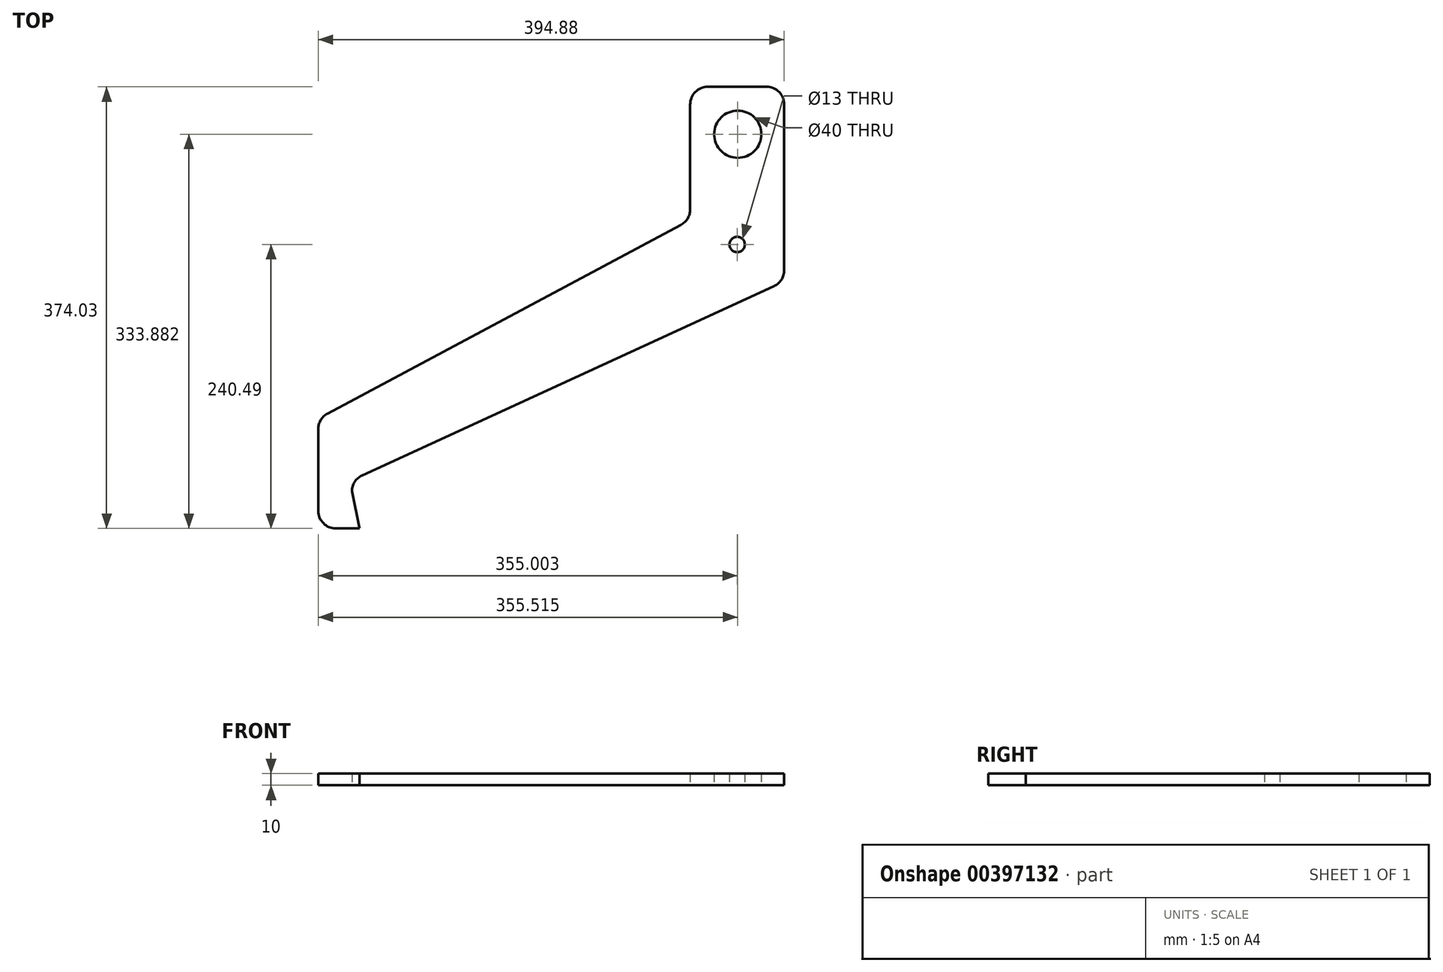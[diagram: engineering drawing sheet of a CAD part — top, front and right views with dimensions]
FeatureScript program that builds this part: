
annotation { "Feature Type Name" : "Feature", "Feature Type Description" : "" }
export const myFeature = defineFeature(function(context is Context, id is Id, definition is map)
    precondition{}
    {
        {
            var Q0;
            Q0=qCreatedBy(makeId("Top.planeOp"),FACE);
            var sketch = newSketch(context, id + "F0", { "sketchPlane" : qUnion([Q0])});
            skLineSegment(sketch, "E0.left", {"start": v(210.78, 66.79) * mm, "end": v(188.14, 86.98) * mm, "construction": true});
            skPoint(sketch, "E0.middle", {"position": v(0, 0) * mm});
            skLineSegment(sketch, "E1", {"start": v(-206.28, -210.92) * mm, "end": v(349.58, -210.92) * mm});
            skLineSegment(sketch, "E2", {"start": v(-160.53, -111.6) * mm, "end": v(-160.53, -210.92) * mm});
            skLineSegment(sketch, "E3.bottom", {"start": v(213.87, 220.23) * mm, "end": v(163.87, 220.5) * mm, "construction": true});
            skLineSegment(sketch, "E3.left", {"start": v(228.8, 205.15) * mm, "end": v(228.02, 65.27) * mm, "construction": true});
            skLineSegment(sketch, "E3.right", {"start": v(148.8, 205.6) * mm, "end": v(148.3, 116.66) * mm, "construction": true});
            skLineSegment(sketch, "E4", {"start": v(-158.92, -56.19) * mm, "end": v(140.37, 103.5) * mm});
            skLineSegment(sketch, "E5", {"start": v(-129.58, -108.53) * mm, "end": v(219.29, 51.72) * mm});
            skLineSegment(sketch, "E6", {"start": v(148.3, 116.66) * mm, "end": v(148.3, 205.52) * mm});
            skLineSegment(sketch, "E7", {"start": v(163.3, 220.52) * mm, "end": v(213.02, 220.52) * mm});
            skLineSegment(sketch, "E8", {"start": v(228.02, 205.52) * mm, "end": v(228.02, 65.27) * mm});
            skCircle(sketch, "E9", {"center": v(188.66, 180.37) * mm, "radius": 20 * mm});
            skLineSegment(sketch, "E10", {"start": v(-166.86, -69.42) * mm, "end": v(-166.86, -138.5) * mm});
            skLineSegment(sketch, "E11", {"start": v(-151.86, -153.5) * mm, "end": v(-142.06, -153.5) * mm});
            skCircle(sketch, "E12", {"center": v(188.14, 86.98) * mm, "radius": 6.5 * mm});
            skArc(sketch, "E13.filletArc", {"start": v(219.29, 51.72) * mm, "mid": v(225.63, 57.22) * mm, "end": v(228.02, 65.27) * mm});
            skArc(sketch, "E14.filletArc", {"start": v(140.37, 103.5) * mm, "mid": v(146.15, 108.99) * mm, "end": v(148.3, 116.66) * mm});
            skArc(sketch, "E15.filletArc", {"start": v(-158.92, -56.19) * mm, "mid": v(-164.72, -61.7) * mm, "end": v(-166.86, -69.42) * mm});
            skArc(sketch, "E16.filletArc", {"start": v(-129.58, -108.53) * mm, "mid": v(-135.86, -113.93) * mm, "end": v(-138.31, -121.85) * mm});
            skArc(sketch, "E17.filletArc", {"start": v(163.3, 220.52) * mm, "mid": v(152.7, 216.13) * mm, "end": v(148.3, 205.52) * mm});
            skArc(sketch, "E18.filletArc", {"start": v(228.02, 205.52) * mm, "mid": v(223.63, 216.13) * mm, "end": v(213.02, 220.52) * mm});
            skArc(sketch, "E19.filletArc", {"start": v(-166.86, -138.5) * mm, "mid": v(-162.46, -149.11) * mm, "end": v(-151.86, -153.5) * mm});
            skLineSegment(sketch, "E20", {"start": v(188.14, 86.98) * mm, "end": v(188.14, -254.15) * mm, "construction": true});
            skLineSegment(sketch, "E21", {"start": v(-138.31, -121.85) * mm, "end": v(-131.86, -153.5) * mm});
            skLineSegment(sketch, "E22", {"start": v(-131.86, -153.5) * mm, "end": v(-142.06, -153.5) * mm});
            skPoint(sketch, "E23.orphan", {"position": v(326.96, 263.67) * mm});
            skLineSegment(sketch, "E24", {"start": v(140.24, 103.44) * mm, "end": v(167.79, 117.48) * mm, "construction": true});
            skPoint(sketch, "E25.orphan", {"position": v(215.76, 62.35) * mm});
            skPoint(sketch, "E26.orphan", {"position": v(160.53, 111.6) * mm});
            skLineSegment(sketch, "E27", {"start": v(188.14, 86.98) * mm, "end": v(206.94, 46.05) * mm, "construction": true});
            skLineSegment(sketch, "E28", {"start": v(188.14, 86.98) * mm, "end": v(167.79, 117.48) * mm, "construction": true});
            skSolve(sketch);
        }
        {
            var Q0;
            Q0 = qSketchRegion(id + "F0", true);
            extrude(context, id + "F1", {"entities" : qUnion([Q0]), "depth" : 10 * mm, "offsetDistance" : 25 * mm});
        }
    });
